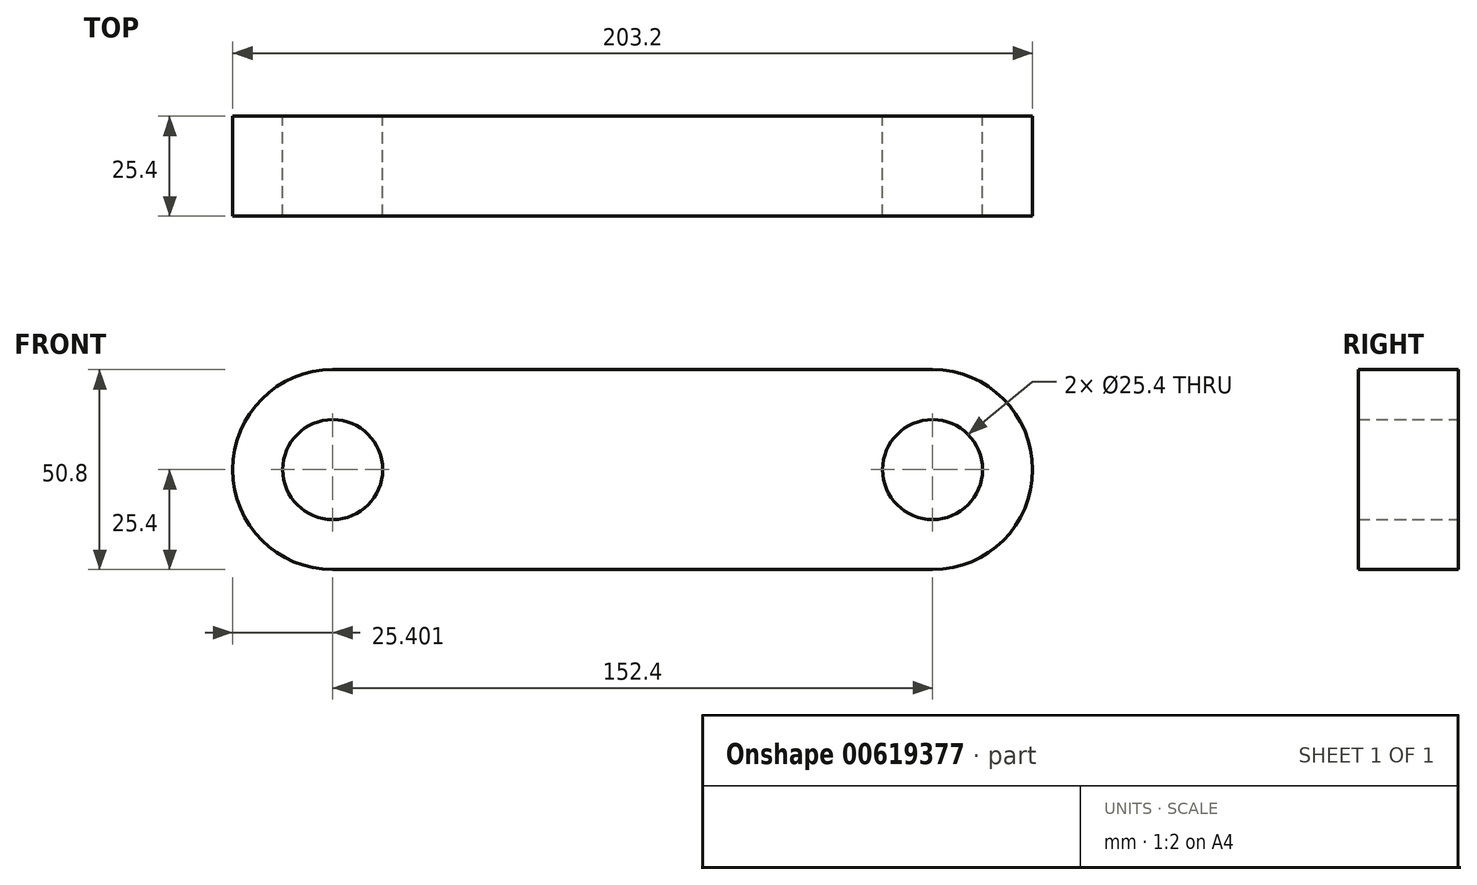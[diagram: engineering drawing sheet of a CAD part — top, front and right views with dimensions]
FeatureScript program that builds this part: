
annotation { "Feature Type Name" : "Feature", "Feature Type Description" : "" }
export const myFeature = defineFeature(function(context is Context, id is Id, definition is map)
    precondition{}
    {
        {
            var Q0;
            Q0=qCreatedBy(makeId("Front.planeOp"),FACE);
            var sketch = newSketch(context, id + "F0", { "sketchPlane" : qUnion([Q0])});
            skLineSegment(sketch, "E0", {"start": v(-16.34, 50.8) * mm, "end": v(136.06, 50.8) * mm});
            skLineSegment(sketch, "E1", {"start": v(-16.34, 0) * mm, "end": v(136.06, 0) * mm});
            skArc(sketch, "E2", {"start": v(-16.34, 50.8) * mm, "mid": v(-41.74, 25.4) * mm, "end": v(-16.34, 0) * mm});
            skArc(sketch, "E3", {"start": v(136.06, 0) * mm, "mid": v(161.46, 25.4) * mm, "end": v(136.06, 50.8) * mm});
            skCircle(sketch, "E4", {"center": v(-16.34, 25.4) * mm, "radius": 12.7 * mm});
            skCircle(sketch, "E5", {"center": v(136.06, 25.4) * mm, "radius": 12.7 * mm});
            skSolve(sketch);
        }
        {
            var Q0;
            Q0=makeQuery(id+"F0.imprint","IMPRINT",FACE,{"disambiguationData":[TD([[makeQuery(id+"F0.imprint","IMPRINT",EDGE,{"derivedFrom":sQuery(id+"F0.wireOp",EDGE,"E0")}),-1.0]])]});
            extrude(context, id + "F1", {"entities" : qUnion([Q0]), "depth" : 25.4 * mm, "offsetDistance" : 25.4 * mm});
        }
    });
